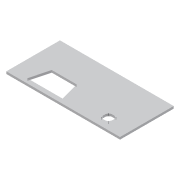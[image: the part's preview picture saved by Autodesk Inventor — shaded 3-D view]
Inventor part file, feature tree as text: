
AUTODESK INVENTOR PART (.ipt)
format: ipt  version: 2016 (Build 200138000, 138)  size: 109,568 bytes
history: native  units: mm
features: sketch x3, extrude x2, hole x1
ambient origin geometry x8: Origin, YZ Plane, XZ Plane, XY Plane, X Axis, Y Axis, Z Axis, Center Point
bodies: Volumenkörper1 (feature_tree)
feature tree (6):
  extrude  "Extrusion1"  Depth=240.0mm
  extrude  "Extrusion2"  Depth=10.0mm
  hole  "Bohrung3"  [1 undecoded]
  sketch  "Skizze1"  dims[d0=500.0mm d1=240.0mm]
  sketch  "Skizze2"  dims[d2=10.0mm d3=0.0mm d25=155.0mm]
  sketch  "Skizze3"  dims[d26=110.0mm d27=150.0mm d28=20.0mm d29=85.0mm d30=10.0mm d31=0.0mm d32=38.0mm d33=100.0mm d34=50.0mm d35=32.0mm d36=32.0mm d37=2.459mm d38=6.0mm d39=4.0mm d40=2.0mm d41=90.0deg d42=8.0mm d43=20.594885mm d47=38.0mm d48=20.0mm]
note: 1 required parameter value undecoded (feature->parameter linkage not recoverable at this tier; creation-order binding heuristic only, values carry confidence <= 0.55)
